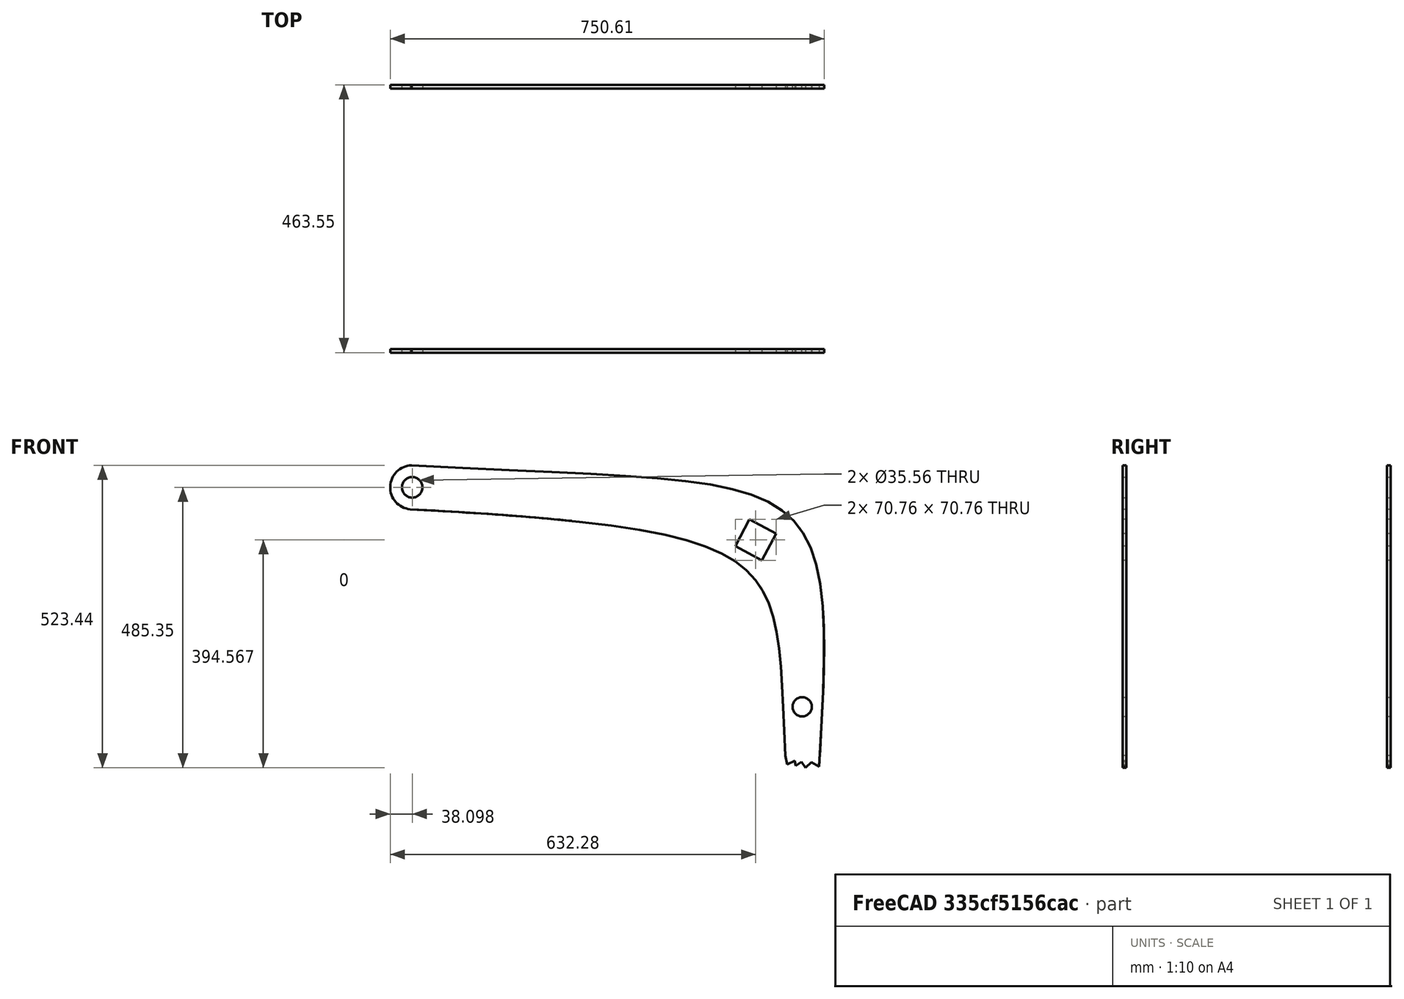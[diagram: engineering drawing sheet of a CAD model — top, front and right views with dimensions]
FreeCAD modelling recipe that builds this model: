
FCSTD DOCUMENT  (FreeCAD 0.17R13522 (Git))
Label: Lid_Plate
License: CreativeCommons Attribution
LicenseURL: http://creativecommons.org/licenses/by/4.0/
objects: Sketcher::SketchObject×1, PartDesign::Pad×1, PartDesign::Body×1, Part::FeaturePython×1
note: 5 computed .brp shape members not serialized (recipe doc carries the construction recipe); baked Part::Feature solids carry a one-line shape summary decoded from their .brp

FEATURE [Sketcher::SketchObject] Sketch001
  MapMode = 5
  Placement = pos=(0,0,0) rot=(1,0,0;1.5708rad)
  sketch-geometry (27):
    g0: Circle [constr] CenterX=287.306 CenterY=468.779 CenterZ=0 NormalX=0 NormalY=0 NormalZ=1 AngleXU=0 Radius=1
    g1: Circle [constr] CenterX=966.82 CenterY=431.461 CenterZ=0 NormalX=0 NormalY=0 NormalZ=1 AngleXU=0 Radius=1
    g2: Circle [constr] CenterX=917.192 CenterY=388.05 CenterZ=0 NormalX=0 NormalY=0 NormalZ=1 AngleXU=0 Radius=1
    g3: BSplineCurve PolesCount=4 KnotsCount=2 Degree=3 IsPeriodic=0
    g4: GeomPoint [constr] X=287.306 Y=468.779 Z=0
    g5: GeomPoint [constr] X=936.124 Y=42.4725 Z=0
    g6-g9: Circle [constr] x4 (B-spline internal-alignment scaffolding for g10; pole/knot coordinates omitted)
    g10: BSplineCurve PolesCount=4 KnotsCount=2 Degree=3 IsPeriodic=0
    g11: GeomPoint [constr] X=289.866 Y=544.821 Z=0
    g12: GeomPoint [constr] X=994.453 Y=23.4664 Z=0
    g13: ArcOfCircle CenterX=290.678 CenterY=506.73 CenterZ=0 NormalX=0 NormalY=0 NormalZ=1 AngleXU=0 Radius=38.1 StartAngle=1.59211 EndAngle=4.62377
    g14: Circle CenterX=290.678 CenterY=506.73 CenterZ=0 NormalX=0 NormalY=0 NormalZ=1 AngleXU=0 Radius=17.78
    g15: LineSegment StartX=849.478 StartY=405.13 StartZ=0 EndX=874.042 EndY=451.329 EndZ=0
    g16: LineSegment StartX=874.042 StartY=451.329 StartZ=0 EndX=920.242 EndY=426.765 EndZ=0
    g17: LineSegment StartX=920.242 StartY=426.765 StartZ=0 EndX=895.677 EndY=380.565 EndZ=0
    g18: LineSegment StartX=895.677 StartY=380.565 StartZ=0 EndX=849.478 EndY=405.13 EndZ=0
    g19: Circle CenterX=965.2 CenterY=127 CenterZ=0 NormalX=0 NormalY=0 NormalZ=1 AngleXU=0 Radius=16.7005
    g20: LineSegment StartX=994.453 StartY=23.4664 StartZ=0 EndX=981.124 EndY=30.9641 EndZ=0
    g21: LineSegment StartX=981.124 StartY=30.9641 StartZ=0 EndX=970.919 EndY=21.3837 EndZ=0
    g22: LineSegment StartX=970.919 StartY=21.3837 StartZ=0 EndX=964.046 EndY=31.5889 EndZ=0
    g23: LineSegment StartX=964.046 StartY=31.5889 StartZ=0 EndX=953.632 EndY=24.716 EndZ=0
    g24: LineSegment StartX=953.632 StartY=24.716 StartZ=0 EndX=952.345 EndY=33.2765 EndZ=0
    g25: LineSegment StartX=952.345 StartY=33.2765 StartZ=0 EndX=939.16 EndY=26.9132 EndZ=0
    g26: LineSegment StartX=939.16 StartY=26.9132 StartZ=0 EndX=936.124 EndY=42.4725 EndZ=0
  constraints (44):
    c: Equal(g0,g1)
    c: Equal(g0,g2)
    c: InternalAlignment(g0,g3)
    c: InternalAlignment(g1,g3)
    c: InternalAlignment(g2,g3)
    c: InternalAlignment(g4,g3)
    c: InternalAlignment(g5,g3)
    c: Equal(g6,g7)
    c: Equal(g6,g8)
    c: Equal(g6,g9)
    c: InternalAlignment(g6-g9 -> g10) x4
    c: InternalAlignment(g11,g10)
    c: InternalAlignment(g12,g10)
    c: Coincident(g13,g6)
    c: Coincident(g13,g0)
    c: Radius(g14) = 17.78
    c: Coincident(g14,g13)
    c: Coincident(g15,g16)
    c: Coincident(g16,g17)
    c: Coincident(g17,g18)
    c: Coincident(g18,g15)
    c: Equal(g16,g17)
    c: DistanceX(g13) = 290.678
    c: DistanceY(g13) = 506.73
    c: Parallel(g15,g17)
    c: Parallel(g16,g18)
    c: Perpendicular(g16,g15)
    c: Distance(g17) = 52.324
    c: Angle(g17,g-1) = 2.05949
    c: DistanceX(g13,g15) = 558.8
    c: DistanceY(g15,g13) = 101.6
    c: Radius(g19) = 16.7005
    c: Coincident(g20,g9)
    c: Coincident(g21,g22)
    c: Coincident(g22,g23)
    c: Coincident(g23,g24)
    c: Coincident(g24,g25)
    c: Coincident(g25,g26)
    c: PointOnObject(g26,g3)
    c: Coincident(g26,g3)
    c: Radius(g13) = 38.1
    c: DistanceX(g19) = 965.2
    c: DistanceY(g19) = 127
    c: Coincident(g20,g21)
FEATURE [PartDesign::Pad] Pad
  Length = 6.35
  Length2 = 100.076
  Placement = pos=(0,0,0) rot=(1,0,0;1.5708rad)
  Profile = -> Sketch001
  Type = 0
FEATURE [PartDesign::Body] Body
  Group = -> [Sketch001,Pad]
  Origin = -> Origin
  Tip = -> Pad
FEATURE [Part::FeaturePython] Array  # Draft array (typed FeaturePython)
  Angle = 360
  ArrayType = 0
  Axis = (0,0,1)
  Base = -> Body
  Center = (0,0,0)
  Fuse = false
  IntervalAxis = (0,0,0)
  IntervalX = (1,0,0)
  IntervalY = (0,457.2,0)
  IntervalZ = (0,0,0)
  NumberPolar = 1
  NumberX = 1
  NumberY = 2
  NumberZ = 1
